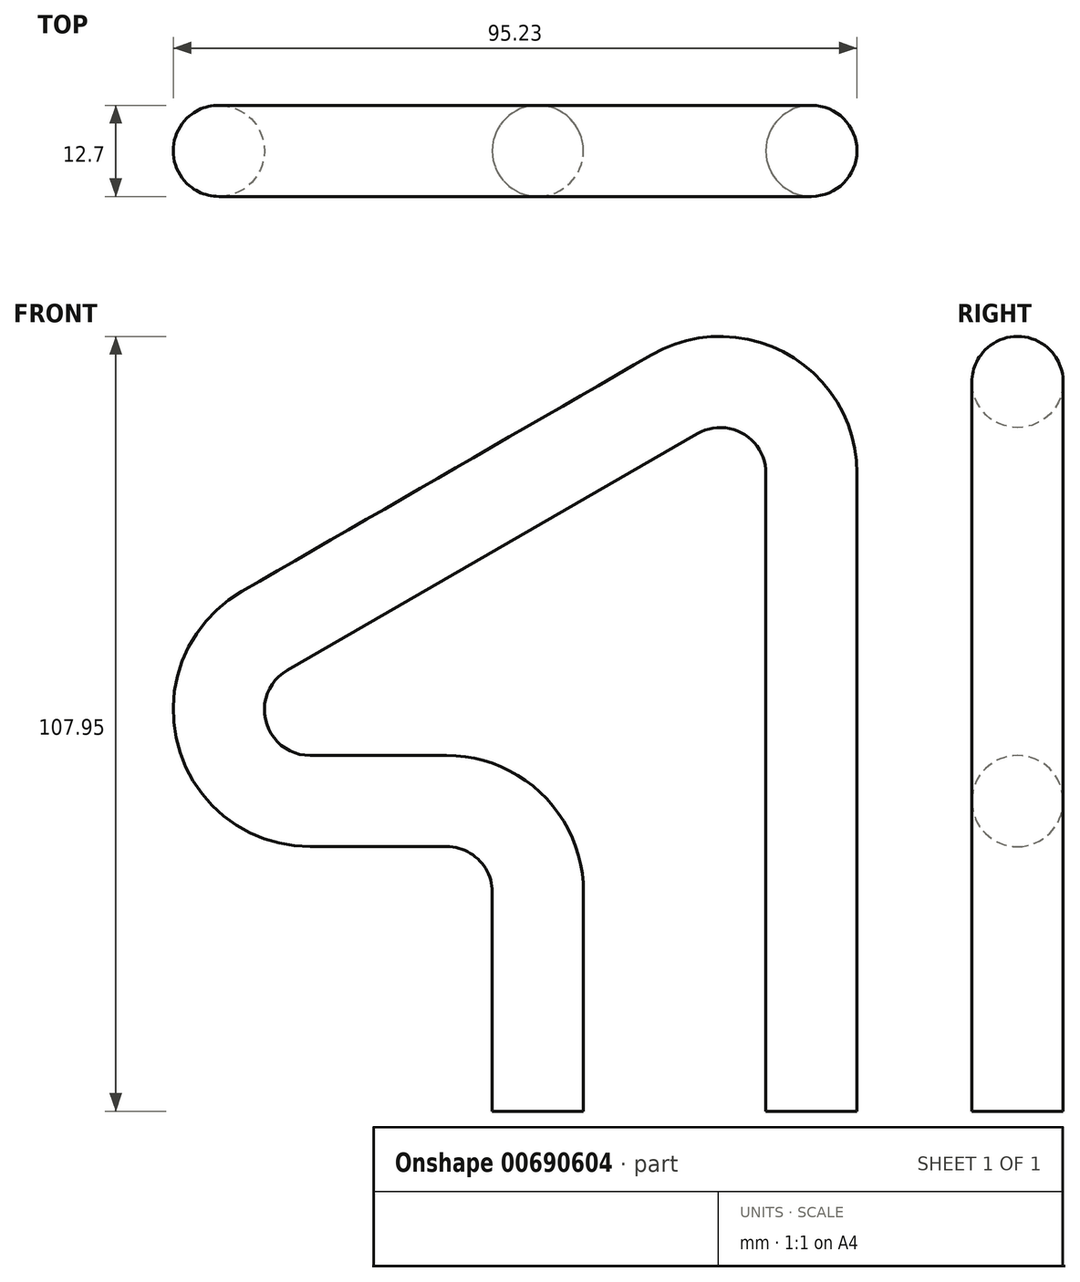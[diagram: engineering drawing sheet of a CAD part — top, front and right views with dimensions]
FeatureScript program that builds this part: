
annotation { "Feature Type Name" : "Feature", "Feature Type Description" : "" }
export const myFeature = defineFeature(function(context is Context, id is Id, definition is map)
    precondition{}
    {
        {
            var Q0;
            Q0=qCreatedBy(makeId("Front.planeOp"),FACE);
            var sketch = newSketch(context, id + "F0", { "sketchPlane" : qUnion([Q0])});
            skLineSegment(sketch, "E0", {"start": v(0, 0) * mm, "end": v(0, 88.9) * mm});
            skLineSegment(sketch, "E1", {"start": v(-19.05, 99.9) * mm, "end": v(-76.18, 66.91) * mm});
            skLineSegment(sketch, "E2", {"start": v(-69.83, 43.21) * mm, "end": v(-50.8, 43.21) * mm});
            skLineSegment(sketch, "E3", {"start": v(-38.1, 30.51) * mm, "end": v(-38.1, 0) * mm});
            skPoint(sketch, "E4.visualSharp", {"position": v(0, 110.9) * mm});
            skArc(sketch, "E4.filletArc", {"start": v(0, 88.9) * mm, "mid": v(-6.35, 99.9) * mm, "end": v(-19.05, 99.9) * mm});
            skPoint(sketch, "E5.visualSharp", {"position": v(-117.23, 43.21) * mm});
            skArc(sketch, "E5.filletArc", {"start": v(-76.18, 66.91) * mm, "mid": v(-82.1, 52.63) * mm, "end": v(-69.83, 43.21) * mm});
            skLineSegment(sketch, "E6", {"start": v(-56.76, 101.6) * mm, "end": v(8.32, 101.6) * mm, "construction": true});
            skPoint(sketch, "E7.visualSharp", {"position": v(-38.1, 43.21) * mm});
            skArc(sketch, "E7.filletArc", {"start": v(-38.1, 30.51) * mm, "mid": v(-41.82, 39.5) * mm, "end": v(-50.8, 43.21) * mm});
            skSolve(sketch);
        }
        {
            var Q0;
            Q0=sQuery(id+"F0.wireOp",VERTEX,"E0.start");
            var Q1;
            Q1=sQuery(id+"F0.wireOp",EDGE,"E0");
            cPlane(context, id + "F1", {"entities" : qUnion([Q0, Q1]), "cplaneType" : CPlaneType.LINE_POINT, "offset" : 25.4 * mm, "width" : 152.4 * mm, "height" : 152.4 * mm});
        }
        {
            var Q0;
            Q0=qCreatedBy(id+"F1.planeOp",FACE);
            var sketch = newSketch(context, id + "F2", { "sketchPlane" : qUnion([Q0])});
            skCircle(sketch, "E8", {"center": v(0, 0) * mm, "radius": 6.35 * mm});
            skSolve(sketch);
        }
        {
            var Q0;
            Q0=makeQuery(id+"F2.imprint","IMPRINT",FACE,{"disambiguationData":[TD([[makeQuery(id+"F2.imprint","IMPRINT",EDGE,{"derivedFrom":sQuery(id+"F2.wireOp",EDGE,"E8")}),1.0]])]});
            var Q1;
            Q1=sQuery(id+"F0.wireOp",EDGE,"E0");
            var Q2;
            Q2=sQuery(id+"F0.wireOp",EDGE,"E4.filletArc");
            var Q3;
            Q3=sQuery(id+"F0.wireOp",EDGE,"E1");
            var Q4;
            Q4=sQuery(id+"F0.wireOp",EDGE,"E5.filletArc");
            var Q5;
            Q5=sQuery(id+"F0.wireOp",EDGE,"E2");
            var Q6;
            Q6=sQuery(id+"F0.wireOp",EDGE,"E7.filletArc");
            var Q7;
            Q7=sQuery(id+"F0.wireOp",EDGE,"E3");
            sweep(context, id + "F3", {"profiles" : qUnion([Q0]), "path" : qUnion([Q1, Q2, Q3, Q4, Q5, Q6, Q7])});
        }
    });
